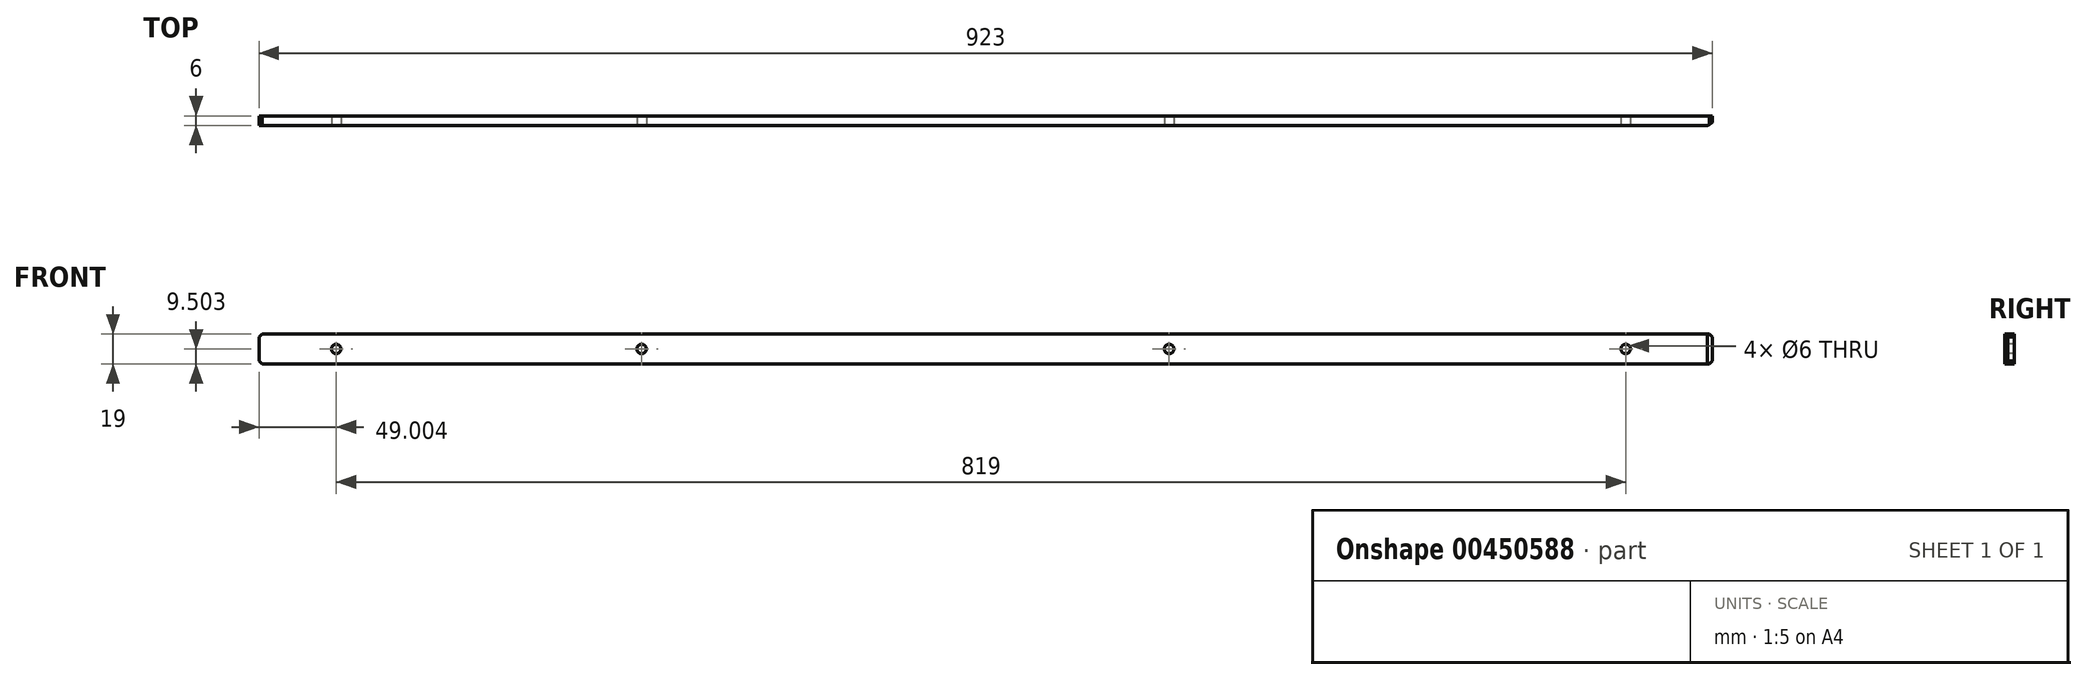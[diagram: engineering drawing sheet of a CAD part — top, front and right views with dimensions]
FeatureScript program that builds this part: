
annotation { "Feature Type Name" : "Feature", "Feature Type Description" : "" }
export const myFeature = defineFeature(function(context is Context, id is Id, definition is map)
    precondition{}
    {
        {
            var Q0;
            Q0=qCreatedBy(makeId("Front.planeOp"),FACE);
            var sketch = newSketch(context, id + "F0", { "sketchPlane" : qUnion([Q0])});
            skLineSegment(sketch, "E0", {"start": v(-643.15, -67.63) * mm, "end": v(275.85, -67.63) * mm});
            skLineSegment(sketch, "E1", {"start": v(-645.15, -65.63) * mm, "end": v(-643.15, -67.63) * mm});
            skLineSegment(sketch, "E2", {"start": v(277.85, -65.63) * mm, "end": v(275.85, -67.63) * mm});
            skLineSegment(sketch, "E3", {"start": v(-643.15, -48.63) * mm, "end": v(275.85, -48.63) * mm});
            skLineSegment(sketch, "E4", {"start": v(277.85, -50.63) * mm, "end": v(275.85, -48.63) * mm});
            skLineSegment(sketch, "E5", {"start": v(-645.15, 164.86) * mm, "end": v(272.66, 164.86) * mm});
            skLineSegment(sketch, "E6", {"start": v(-645.15, 170.86) * mm, "end": v(277.85, 170.86) * mm});
            skLineSegment(sketch, "E7", {"start": v(272.66, 164.86) * mm, "end": v(277.85, 167.86) * mm});
            skLineSegment(sketch, "E8", {"start": v(-645.15, -50.63) * mm, "end": v(-645.15, -65.63) * mm});
            skLineSegment(sketch, "E9", {"start": v(-643.15, -48.63) * mm, "end": v(-645.15, -50.63) * mm});
            skLineSegment(sketch, "E10", {"start": v(277.85, -65.63) * mm, "end": v(277.85, -50.63) * mm});
            skLineSegment(sketch, "E11", {"start": v(-645.15, 170.86) * mm, "end": v(-645.15, 164.86) * mm});
            skLineSegment(sketch, "E12", {"start": v(277.85, 170.86) * mm, "end": v(277.85, 167.86) * mm});
            skLineSegment(sketch, "E13", {"start": v(227.35, -58.13) * mm, "end": v(218.35, -58.13) * mm});
            skCircle(sketch, "E14", {"center": v(222.85, -58.13) * mm, "radius": 3 * mm});
            skLineSegment(sketch, "E15", {"start": v(222.85, -62.63) * mm, "end": v(222.85, -53.63) * mm});
            skCircle(sketch, "E16", {"center": v(222.85, -58.13) * mm, "radius": 2.46 * mm});
            skLineSegment(sketch, "E17", {"start": v(-62.65, -58.13) * mm, "end": v(-71.65, -58.13) * mm});
            skCircle(sketch, "E18", {"center": v(-67.15, -58.13) * mm, "radius": 3 * mm});
            skLineSegment(sketch, "E19", {"start": v(-67.15, -62.63) * mm, "end": v(-67.15, -53.63) * mm});
            skCircle(sketch, "E20", {"center": v(-67.15, -58.13) * mm, "radius": 2.46 * mm});
            skLineSegment(sketch, "E21", {"start": v(-397.65, -58.13) * mm, "end": v(-406.65, -58.13) * mm});
            skCircle(sketch, "E22", {"center": v(-402.15, -58.13) * mm, "radius": 3 * mm});
            skLineSegment(sketch, "E23", {"start": v(-402.15, -62.63) * mm, "end": v(-402.15, -53.63) * mm});
            skCircle(sketch, "E24", {"center": v(-402.15, -58.13) * mm, "radius": 2.46 * mm});
            skLineSegment(sketch, "E25", {"start": v(-591.65, -58.13) * mm, "end": v(-600.65, -58.13) * mm});
            skCircle(sketch, "E26", {"center": v(-596.15, -58.13) * mm, "radius": 3 * mm});
            skLineSegment(sketch, "E27", {"start": v(-596.15, -62.63) * mm, "end": v(-596.15, -53.63) * mm});
            skCircle(sketch, "E28", {"center": v(-596.15, -58.13) * mm, "radius": 2.46 * mm});
            skSolve(sketch);
        }
        {
            var Q0;
            Q0=makeQuery(id+"F0.imprint","IMPRINT",FACE,{"disambiguationData":[TD([[makeQuery(id+"F0.imprint","IMPRINT",EDGE,{"derivedFrom":sQuery(id+"F0.wireOp",EDGE,"E0")}),1.0]])]});
            extrude(context, id + "F1", {"entities" : qUnion([Q0]), "oppositeDirection" : true, "depth" : 6 * mm});
        }
        {
            var Q0;
            Q0=makeQuery(id+"F1.opExtrude","CAP_EDGE",EDGE,{"disambiguationData":[OSD([sQuery(id+"F0.wireOp",EDGE,"E10")])],"isStart":true});
            chamfer(context, id + "F2", {"entities" : qUnion([Q0]), "chamferType" : ChamferType.OFFSET_ANGLE, "width" : 3 * mm, "oppositeDirection" : false, "angle" : 30 * degree, "tangentPropagation" : true});
        }
    });
